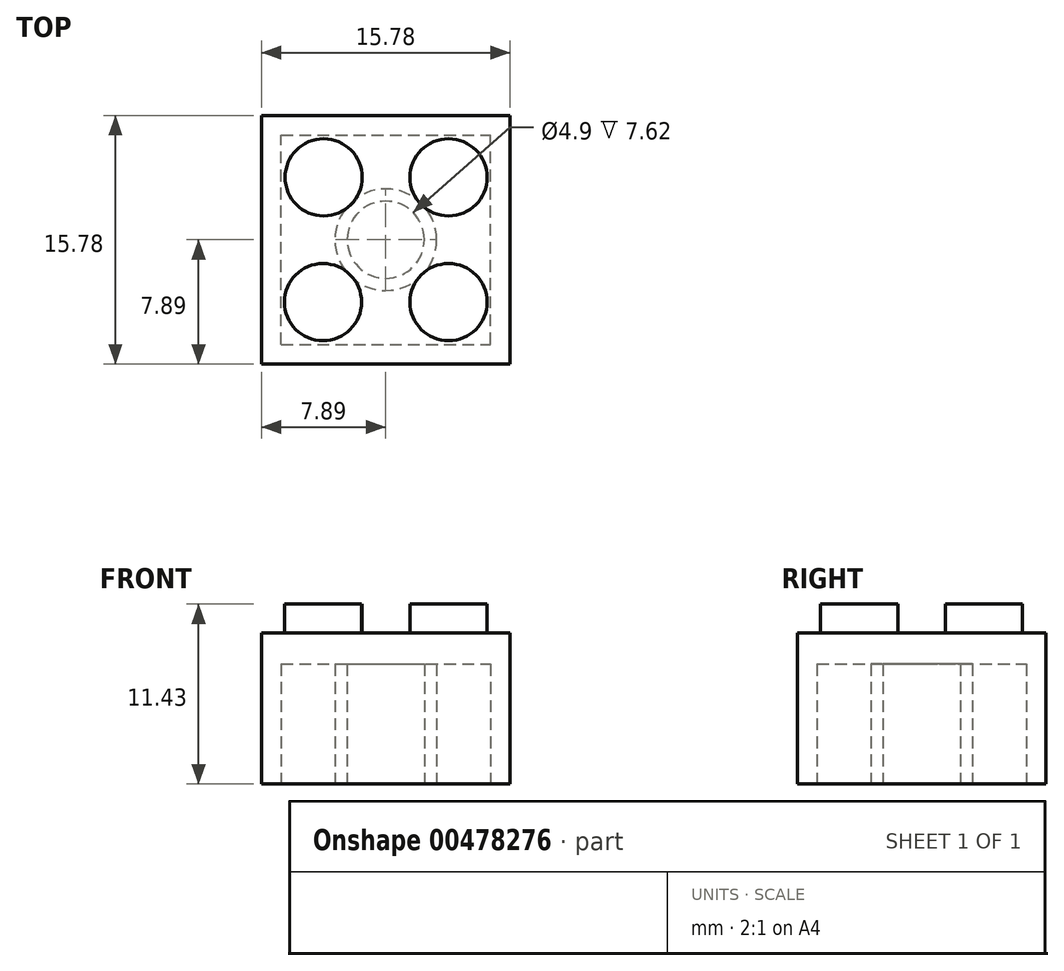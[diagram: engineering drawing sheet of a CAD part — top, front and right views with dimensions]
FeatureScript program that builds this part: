
annotation { "Feature Type Name" : "Feature", "Feature Type Description" : "" }
export const myFeature = defineFeature(function(context is Context, id is Id, definition is map)
    precondition{}
    {
        {
            var Q0;
            Q0=qCreatedBy(makeId("Top.planeOp"),FACE);
            var sketch = newSketch(context, id + "F0", { "sketchPlane" : qUnion([Q0])});
            skLineSegment(sketch, "E0.bottom", {"start": v(-7.89, 7.89) * mm, "end": v(7.89, 7.89) * mm});
            skLineSegment(sketch, "E0.top", {"start": v(-7.89, -7.89) * mm, "end": v(7.89, -7.89) * mm});
            skLineSegment(sketch, "E0.left", {"start": v(-7.89, 7.89) * mm, "end": v(-7.89, -7.89) * mm});
            skLineSegment(sketch, "E0.right", {"start": v(7.89, 7.89) * mm, "end": v(7.89, -7.89) * mm});
            skPoint(sketch, "E0.middle", {"position": v(0, 0) * mm});
            skSolve(sketch);
        }
        {
            var Q0;
            Q0 = qSketchRegion(id + "F0", true);
            extrude(context, id + "F1", {"entities" : qUnion([Q0]), "depth" : 9.6 * mm, "offsetDistance" : 25.4 * mm});
        }
        {
            var Q0;
            Q0=makeQuery(id+"F0.imprint","IMPRINT",FACE,{"disambiguationData":[TD([[makeQuery(id+"F0.imprint","IMPRINT",EDGE,{"derivedFrom":sQuery(id+"F0.wireOp",EDGE,"E0.bottom")}),-1.0]])]});
            var sketch = newSketch(context, id + "F2", { "sketchPlane" : qUnion([Q0])});
            skCircle(sketch, "E1", {"center": v(-3.94, 3.96) * mm, "radius": 2.45 * mm});
            skCircle(sketch, "E2", {"center": v(3.99, 3.96) * mm, "radius": 2.45 * mm});
            skCircle(sketch, "E3", {"center": v(-3.99, -3.96) * mm, "radius": 2.45 * mm});
            skCircle(sketch, "E4", {"center": v(3.99, -3.96) * mm, "radius": 2.45 * mm});
            skSolve(sketch);
        }
        {
            var Q0;
            Q0 = qSketchRegion(id + "F4", true);
            var Q1;
            Q1 = qSketchRegion(id + "F2", true);
            extrude(context, id + "F3", {"entities" : qUnion([Q0, Q1]), "operationType" : NewBodyOperationType.ADD, "depth" : 11.43 * mm, "offsetDistance" : 25.4 * mm});
        }
        {
            var Q0;
            Q0=makeQuery(id+"F1.opExtrude","CAP_FACE",FACE,{"disambiguationData":[OSD([sQuery(id+"F0.wireOp",EDGE,"E0.bottom"),sQuery(id+"F0.wireOp",EDGE,"E0.top"),sQuery(id+"F0.wireOp",EDGE,"E0.left"),sQuery(id+"F0.wireOp",EDGE,"E0.right")])],"isStart":true});
            var sketch = newSketch(context, id + "F4", { "sketchPlane" : qUnion([Q0])});
            skLineSegment(sketch, "E5.bottom", {"start": v(-6.64, 6.64) * mm, "end": v(6.64, 6.64) * mm});
            skLineSegment(sketch, "E5.top", {"start": v(-6.64, -6.64) * mm, "end": v(6.64, -6.64) * mm});
            skLineSegment(sketch, "E5.left", {"start": v(-6.64, 6.64) * mm, "end": v(-6.64, -6.64) * mm});
            skLineSegment(sketch, "E5.right", {"start": v(6.64, 6.64) * mm, "end": v(6.64, -6.64) * mm});
            skPoint(sketch, "E5.middle", {"position": v(0, 0) * mm});
            skCircle(sketch, "E6", {"center": v(0, 0) * mm, "radius": 3.23 * mm});
            skCircle(sketch, "E7", {"center": v(0, 0) * mm, "radius": 2.45 * mm});
            skSolve(sketch);
        }
        {
            var Q0;
            Q0=makeQuery(id+"F4.imprint","IMPRINT",FACE,{"disambiguationData":[TD([[makeQuery(id+"F4.imprint","IMPRINT",EDGE,{"derivedFrom":sQuery(id+"F4.wireOp",EDGE,"E5.bottom")}),-1.0]])]});
            extrude(context, id + "F5", {"entities" : qUnion([Q0]), "operationType" : NewBodyOperationType.REMOVE, "oppositeDirection" : true, "depth" : 7.62 * mm, "offsetDistance" : 25.4 * mm});
        }
        {
            var Q0;
            Q0=makeQuery(id+"F5.boolean.opBoolean","SPLIT",FACE,{"disambiguationData":[TD([makeQuery(id+"F5.opExtrude","SWEPT_FACE",FACE,{"disambiguationData":[OSD([sQuery(id+"F4.wireOp",EDGE,"E6")])]})])],"derivedFrom":makeQuery(id+"F1.opExtrude","CAP_FACE",FACE,{"disambiguationData":[OSD([sQuery(id+"F0.wireOp",EDGE,"E0.bottom"),sQuery(id+"F0.wireOp",EDGE,"E0.top"),sQuery(id+"F0.wireOp",EDGE,"E0.left"),sQuery(id+"F0.wireOp",EDGE,"E0.right")])],"isStart":true})});
            var sketch = newSketch(context, id + "F6", { "sketchPlane" : qUnion([Q0])});
            skCircle(sketch, "E8", {"center": v(0, 0) * mm, "radius": 2.45 * mm});
            skSolve(sketch);
        }
        {
            var Q0;
            Q0=makeQuery(id+"F6.imprint","IMPRINT",FACE,{"disambiguationData":[TD([[makeQuery(id+"F6.imprint","IMPRINT",EDGE,{"derivedFrom":sQuery(id+"F6.wireOp",EDGE,"E8")}),1.0]])]});
            extrude(context, id + "F7", {"entities" : qUnion([Q0]), "operationType" : NewBodyOperationType.REMOVE, "oppositeDirection" : true, "depth" : 7.62 * mm, "offsetDistance" : 25.4 * mm});
        }
    });
